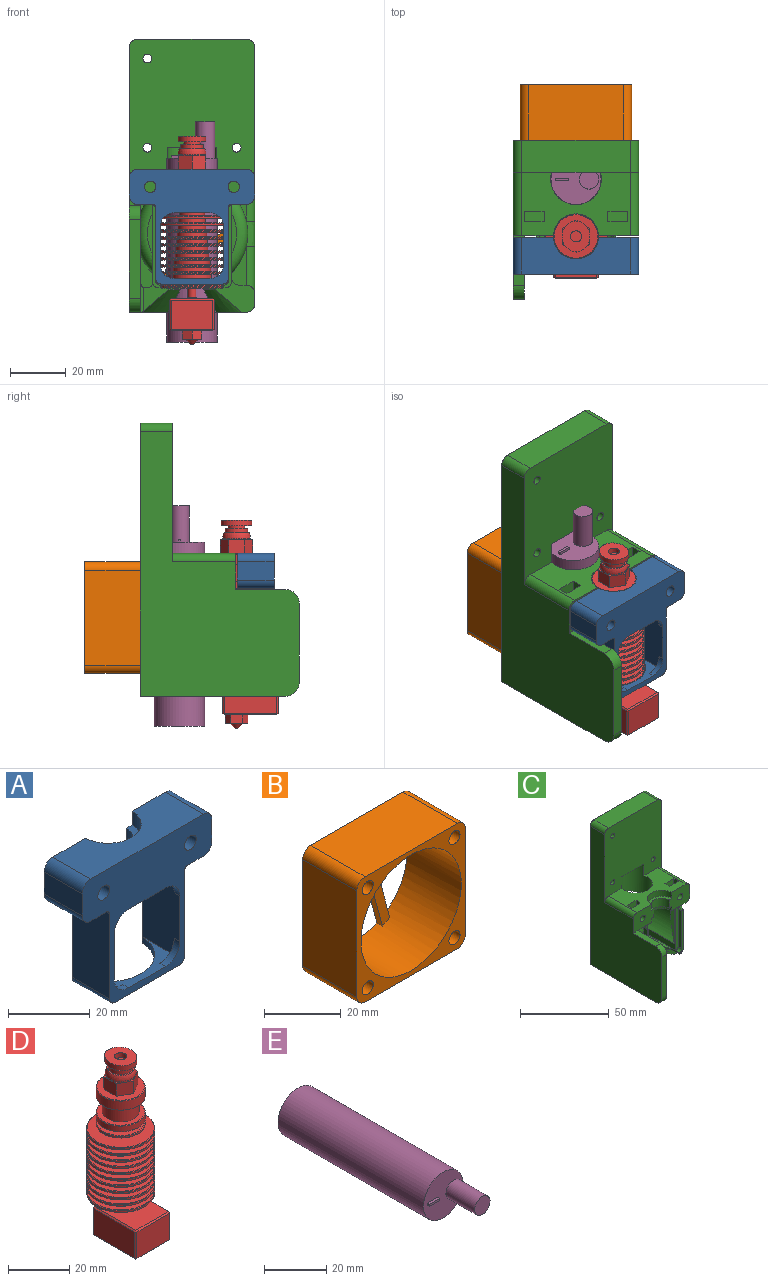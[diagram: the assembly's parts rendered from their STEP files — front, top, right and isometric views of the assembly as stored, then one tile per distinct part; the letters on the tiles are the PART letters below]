
ASSEMBLY  parts=5 mates=8
PART A: 39 faces, bbox 45x13.2x41.2 mm
  f0: plane 5x5mm, normal (0,1,0), area 5.4mm2, adj f15,f24,f26
  f1: plane 26.6x13mm, normal (1,0,0), area 319.8mm2, adj f2,f20,f21,f23,f24,f25,f27,f29
  f2: plane 39x13.2mm, normal (0,0,-1), area 303.4mm2, adj f1,f6,f11,f12,f15,f18,f20,f21
  f3: plane 39x13.2mm, normal (0,0,1), area 416.6mm2, adj f10,f11,f12,f21,f32,f33
  f4: plane 13.2x6.6mm, normal (1,0,0), area 87.1mm2, adj f11,f21,f31,f32
  f5: plane 13.2x6.6mm, normal (-1,0,0), area 87.1mm2, adj f12,f21,f33,f34
  f6: cylinder r=8.1mm len=16.19mm, axis (0,0,-1), area 67.1mm2, adj f2,f7,f11,f12
  f7: plane 16.19x7.8mm, normal (0,0,-1), area 43.4mm2, adj f6,f8,f11,f12
  f8: cylinder r=6.1mm len=12.19mm, axis (0,0,-1), area 107.7mm2, adj f7,f9,f11,f12
  f9: plane 16.19x7.8mm, normal (0,0,1), area 43.4mm2, adj f8,f10,f11,f12
  f10: cylinder r=8.1mm len=16.19mm, axis (0,0,-1), area 101.9mm2, adj f3,f9,f11,f12
  f11: plane 16.41x12.6mm, normal (0,1,0), area 176.1mm2, adj f2,f3,f4,f6,f7,f8,f9,f10
  f12: plane 16.41x12.6mm, normal (0,1,0), area 176.1mm2, adj f2,f3,f5,f6,f7,f8,f9,f10
  f13: cylinder r=2.05mm len=13.2mm, axis (0,-1,0), area 170mm2, adj f12,f21
  f14: cylinder r=2.05mm len=13.2mm, axis (0,-1,0), area 170mm2, adj f11,f21
  f15: plane 26.6x13mm, normal (-1,0,0), area 319.8mm2, adj f0,f2,f18,f21,f23,f24,f26,f28
  f16: plane 22x10.51mm, normal (0,0,-1), area 94.5mm2, adj f21,f30,f35,f36
  f17: plane 25.6x13mm, normal (1,0,0), area 332.8mm2, adj f18,f21,f36,f38
  f18: plane 28.56x2.61mm, normal (0,1,0), area 45.1mm2, adj f2,f15,f17,f24,f30,f36,f38
  f19: plane 25.6x13mm, normal (-1,0,0), area 332.8mm2, adj f20,f21,f35,f37
  f20: plane 28.56x2.61mm, normal (0,1,0), area 45.1mm2, adj f1,f2,f19,f24,f30,f35,f37
  f21: plane 45x41.2mm, normal (0,-1,0), area 758.6mm2, adj f1,f2,f3,f4,f5,f13,f14,f15
  f22: plane 12.8x2mm, normal (0,0,-1), area 25.6mm2, adj f21,f23,f28,f29
  f23: plane 22.8x8mm, normal (0,1,0), area 79.1mm2, adj f1,f2,f15,f22,f28,f29
  f24: plane 22.8x13mm, normal (0,0,1), area 83.7mm2, adj f0,f1,f15,f18,f20,f21,f25,f26
  f25: plane 5x5mm, normal (0,1,0), area 5.4mm2, adj f1,f24,f27
  f26: cylinder r=5mm len=5mm, axis (0,-1,0), area 15.7mm2, adj f0,f15,f21,f24
  f27: cylinder r=5mm len=5mm, axis (0,1,0), area 15.7mm2, adj f1,f21,f24,f25
  f28: cylinder r=5mm len=5mm, axis (0,1,0), area 15.7mm2, adj f15,f21,f22,f23
  f29: cylinder r=5mm len=5mm, axis (0,-1,0), area 15.7mm2, adj f1,f21,f22,f23
  f30: cylinder r=11.4mm len=22.78mm, axis (0,0,-1), area 69.5mm2, adj f16,f18,f20,f24,f35,f36
  f31: cylinder r=3mm len=13.2mm, axis (0,-1,0), area 62.2mm2, adj f2,f4,f11,f21
  f32: cylinder r=3mm len=13.2mm, axis (0,1,0), area 62.2mm2, adj f3,f4,f11,f21
  f33: cylinder r=3mm len=13.2mm, axis (0,-1,0), area 62.2mm2, adj f3,f5,f12,f21
  f34: cylinder r=3mm len=13.2mm, axis (0,1,0), area 62.2mm2, adj f2,f5,f12,f21
  f35: cylinder r=2mm len=13mm, axis (0,1,0), area 40.2mm2, adj f16,f19,f20,f21,f30
  f36: cylinder r=2mm len=13mm, axis (0,-1,0), area 40.2mm2, adj f16,f17,f18,f21,f30
  f37: cylinder r=1mm len=13mm, axis (0,-1,0), area 20.4mm2, adj f2,f19,f20,f21
  f38: cylinder r=1mm len=13mm, axis (0,1,0), area 20.4mm2, adj f2,f17,f18,f21
PART B: 25 faces, bbox 40x20x40 mm
  f0: plane 34x20mm, normal (0,0,-1), area 680mm2, adj f9,f10,f21,f24
  f1: plane 34x20mm, normal (1,0,0), area 680mm2, adj f9,f10,f21,f22
  f2: plane 34x20mm, normal (0,0,1), area 680mm2, adj f9,f10,f22,f23
  f3: cylinder r=18.5mm len=37mm, axis (0,1,0), area 2306.3mm2, adj f9,f10,f12,f13,f15,f16,f18,f19
  f4: cylinder r=2.05mm len=20mm, axis (0,1,0), area 257.6mm2, adj f9,f10
  f5: cylinder r=2.05mm len=20mm, axis (0,1,0), area 257.6mm2, adj f9,f10
  f6: cylinder r=2.05mm len=20mm, axis (0,1,0), area 257.6mm2, adj f9,f10
  f7: cylinder r=2.05mm len=20mm, axis (0,1,0), area 257.6mm2, adj f9,f10
  f8: plane 34x20mm, normal (-1,0,0), area 680mm2, adj f9,f10,f23,f24
  f9: plane 40x40mm, normal (0,-1,0), area 464.3mm2, adj f0,f1,f2,f3,f4,f5,f6,f7
  f10: plane 40x40mm, normal (0,1,0), area 702.9mm2, adj f0,f1,f2,f3,f4,f5,f6,f7
  f11: cylinder r=6mm len=5.91mm, axis (0,1,0), area 15.5mm2, adj f10,f12,f19,f20
  f12: plane 9.16x9.16mm, normal (0.71,0,-0.71), area 25.9mm2, adj f3,f10,f11,f20
  f13: plane 11.21x11.21mm, normal (-0.71,0,0.71), area 31.7mm2, adj f3,f10,f14,f20
  f14: cylinder r=6mm len=6.56mm, axis (0,1,0), area 15.5mm2, adj f10,f13,f15,f20
  f15: plane 12.52x3.35mm, normal (0.26,0,0.97), area 25.9mm2, adj f3,f10,f14,f20
  f16: plane 15.31x4.1mm, normal (-0.26,0,-0.97), area 31.7mm2, adj f3,f10,f17,f20
  f17: cylinder r=6mm len=7.2mm, axis (0,1,0), area 15.5mm2, adj f10,f16,f18,f20
  f18: plane 12.52x3.35mm, normal (-0.97,0,-0.26), area 25.9mm2, adj f3,f10,f17,f20
  f19: plane 15.31x4.1mm, normal (0.97,0,0.26), area 31.7mm2, adj f3,f10,f11,f20
  f20: plane 33.46x29.5mm, normal (0,-1,0), area 238.6mm2, adj f3,f11,f12,f13,f14,f15,f16,f17
  f21: cylinder r=3mm len=20mm, axis (0,-1,0), area 94.2mm2, adj f0,f1,f9,f10
  f22: cylinder r=3mm len=20mm, axis (0,1,0), area 94.2mm2, adj f1,f2,f9,f10
  f23: cylinder r=3mm len=20mm, axis (0,-1,0), area 94.2mm2, adj f2,f8,f9,f10
  f24: cylinder r=3mm len=20mm, axis (0,1,0), area 94.2mm2, adj f0,f8,f9,f10
PART C: 128 faces, bbox 46.5x61.4x99.5 mm
  f0: plane 11.9x4.4mm, normal (0,-1,0), area 34.1mm2, adj f2,f5,f11,f102,f122,f126
  f1: plane 10.46x9.18mm, normal (0,-1,0), area 42.6mm2, adj f5,f57,f80,f95,f100,f102,f125,f126
  f2: cylinder r=20mm len=22.2mm, axis (0,1,0), area 177mm2, adj f0,f4,f11,f122
  f3: cylinder r=20mm len=22.2mm, axis (0,1,0), area 72.4mm2, adj f4,f13,f14,f122
  f4: torus R=16mm, axis (0,-1,0), area 107.7mm2, adj f2,f3,f11,f13,f15,f20,f76,f99
  f5: plane 18.7x0.4mm, normal (0,0,1), area 7.5mm2, adj f0,f1,f102,f126
  f6: plane 98.6x45.6mm, normal (0,1,0), area 3336.5mm2, adj f8,f18,f38,f39,f61,f62,f63,f64
  f7: plane 39x22.7mm, normal (0,0,1), area 558.1mm2, adj f19,f20,f30,f32,f42,f43,f44,f45
  f8: plane 92x34.2mm, normal (1,0,0), area 979.4mm2, adj f6,f19,f85,f86,f87,f88,f89,f90
  f9: cylinder r=1.6mm len=4.4mm, axis (1,0,0), area 44.2mm2, adj f113,f114
  f10: plane 5x2.15mm, normal (-1,0,0), area 10.7mm2, adj f105,f106,f107,f111
  f11: plane 29.2x27.6mm, normal (-1,0,0), area 175mm2, adj f0,f2,f4,f15,f77,f95,f99,f102
  f12: plane 26.2x0.4mm, normal (1,0,0), area 10.5mm2, adj f13,f14,f20,f82
  f13: plane 26.2x8.43mm, normal (0,0,-1), area 95.2mm2, adj f3,f4,f12,f14,f20
  f14: plane 3.48x2.9mm, normal (0,-1,0), area 2.8mm2, adj f3,f12,f13,f82,f122
  f15: plane 15.13x1.9mm, normal (0,-1,0), area 19.4mm2, adj f4,f11
  f16: plane 15.13x1.9mm, normal (0,-1,0), area 19.4mm2, adj f68,f93
  f17: plane 6.06x2.48mm, normal (0,-1,0), area 6.3mm2, adj f24,f67,f86
  f18: plane 52x42mm, normal (0,0,-1), area 749.4mm2, adj f6,f38,f55,f60,f90,f100,f101,f108
  f19: plane 41.59x16.41mm, normal (0,-1,0), area 226.6mm2, adj f7,f8,f23,f24,f31,f32,f33,f34
  f20: plane 41.59x16.41mm, normal (0,-1,0), area 229.3mm2, adj f4,f7,f12,f13,f23,f32,f33,f34
  f21: plane 3.8x0.1mm, normal (0,1,0), area 0.2mm2, adj f61,f72
  f22: plane 18.7x2.4mm, normal (0,0,1), area 44.9mm2, adj f28,f60,f84,f89
  f23: plane 26.2x23.77mm, normal (0,0,-1), area 292.3mm2, adj f19,f20,f30,f36,f62,f65,f66,f69
  f24: plane 26.2x7.43mm, normal (0,0,-1), area 69mm2, adj f17,f19,f67,f85,f93
  f25: plane 24.37x7.02mm, normal (0,0,1), area 75mm2, adj f26,f55,f56,f57,f97
  f26: plane 4.56x3.93mm, normal (0,-1,0), area 11.3mm2, adj f25,f55,f61,f70,f97
  f27: plane 4.56x3.93mm, normal (0,-1,0), area 11.3mm2, adj f29,f55,f61,f65,f96
  f28: plane 14.06x5.4mm, normal (0,-1,0), area 41.8mm2, adj f22,f67,f68,f84,f88
  f29: plane 24.37x7.02mm, normal (0,0,1), area 75mm2, adj f27,f55,f58,f59,f96
  f30: cylinder r=9.1mm len=20.6mm, axis (0,0,1), area 886.5mm2, adj f7,f23,f62,f116,f127
  f31: cylinder r=2.05mm len=5mm, axis (0,-1,0), area 64.4mm2, adj f19,f46
  f32: cylinder r=8.1mm len=16.19mm, axis (0,0,-1), area 101.9mm2, adj f7,f19,f20,f33
  f33: plane 16.19x7.8mm, normal (0,0,1), area 43.4mm2, adj f19,f20,f32,f34
  f34: cylinder r=6.1mm len=12.19mm, axis (0,0,-1), area 107.7mm2, adj f19,f20,f33,f35
  f35: plane 16.19x7.8mm, normal (0,0,-1), area 43.4mm2, adj f19,f20,f34,f36
  f36: cylinder r=8.1mm len=16.19mm, axis (0,0,-1), area 67.1mm2, adj f19,f20,f23,f35
  f37: plane 10.34x3.7mm, normal (1,0,0), area 36.7mm2, adj f60,f89,f90,f115
  f38: plane 95x57mm, normal (-1,0,0), area 3051.4mm2, adj f6,f18,f20,f82,f83,f92,f116,f117
  f39: plane 39x11.5mm, normal (0,0,1), area 448.5mm2, adj f6,f91,f92,f116
  f40: cylinder r=2.05mm len=5mm, axis (0,-1,0), area 64.4mm2, adj f20,f43
  f41: plane 7.1x3.8mm, normal (0,0,1), area 27mm2, adj f42,f43,f44,f45
  f42: plane 10.8x3.8mm, normal (-1,0,0), area 41mm2, adj f7,f41,f43,f45
  f43: plane 10.8x7.1mm, normal (0,1,0), area 63.5mm2, adj f7,f40,f41,f42,f44
  f44: plane 10.8x3.8mm, normal (1,0,0), area 41mm2, adj f7,f41,f43,f45
  f45: plane 10.8x7.1mm, normal (0,-1,0), area 63.5mm2, adj f7,f41,f42,f44,f52
  f46: plane 10.8x7.1mm, normal (0,1,0), area 63.5mm2, adj f7,f31,f48,f49,f50
  f47: plane 10.8x7.1mm, normal (0,-1,0), area 63.5mm2, adj f7,f48,f49,f50,f54
  f48: plane 7.1x3.8mm, normal (0,0,1), area 27mm2, adj f46,f47,f49,f50
  f49: plane 10.8x3.8mm, normal (1,0,0), area 41mm2, adj f7,f46,f47,f48
  f50: plane 10.8x3.8mm, normal (-1,0,0), area 41mm2, adj f7,f46,f47,f48
  f51: plane 4.1x4.1mm, normal (0,-1,0), area 13.2mm2, adj f52
  f52: cylinder r=2.05mm len=4.1mm, axis (0,-1,0), area 30.9mm2, adj f45,f51
  f53: plane 4.1x4.1mm, normal (0,-1,0), area 13.2mm2, adj f54
  f54: cylinder r=2.05mm len=4.1mm, axis (0,-1,0), area 30.9mm2, adj f47,f53
  f55: cylinder r=9.1mm len=18.2mm, axis (0,0,1), area 333.8mm2, adj f18,f25,f26,f27,f29,f56,f58,f61
  f56: plane 7.52x4.9mm, normal (0.82,0.57,0), area 25.6mm2, adj f25,f55,f57,f100
  f57: cylinder r=11.4mm len=10.61mm, axis (0,0,-1), area 17.2mm2, adj f1,f25,f56,f80,f81,f97,f100
  f58: plane 7.52x4.9mm, normal (-0.82,0.57,0), area 25.6mm2, adj f29,f55,f59,f101
  f59: cylinder r=11.4mm len=10.61mm, axis (0,0,-1), area 17.2mm2, adj f29,f58,f60,f78,f79,f96,f101
  f60: plane 15.69x14.21mm, normal (0,-1,0), area 91.6mm2, adj f18,f22,f37,f59,f68,f78,f84,f89
  f61: cylinder r=18.5mm len=37mm, axis (0,-1,0), area 1412.8mm2, adj f6,f21,f26,f27,f55,f63,f64,f65
  f62: plane 23.77x8mm, normal (0,0.57,-0.82), area 151.8mm2, adj f6,f23,f30,f63,f64
  f63: bspline ~13.74x11.32mm, area 62.1mm2, adj f6,f61,f62,f66
  f64: bspline ~13.74x11.32mm, area 62.1mm2, adj f6,f61,f62,f69
  f65: plane 28.99x26.2mm, normal (-1,0,0), area 132.8mm2, adj f19,f23,f27,f61,f73,f96
  f66: extruded ~24.31x5.61mm, area 150.1mm2, adj f23,f61,f63,f73
  f67: cylinder r=20mm len=24.68mm, axis (0,1,0), area 595.4mm2, adj f17,f24,f28,f68,f87,f93
  f68: plane 29.2x27.6mm, normal (1,0,0), area 137.6mm2, adj f16,f28,f60,f67,f75,f84,f93,f94
  f69: extruded ~24.31x5.61mm, area 155.1mm2, adj f23,f61,f64,f72
  f70: plane 28.99x26.2mm, normal (1,0,0), area 132.8mm2, adj f20,f23,f26,f61,f72,f97
  f71: plane 3.8x0.1mm, normal (0,1,0), area 0.2mm2, adj f61,f73
  f72: plane 26.43x11.36mm, normal (0.82,0.57,0), area 231.6mm2, adj f21,f23,f61,f69,f70
  f73: plane 25.41x10.34mm, normal (-0.82,0.57,0), area 231.6mm2, adj f23,f61,f65,f66,f71
  f74: plane 25.61x3mm, normal (-1,0,0), area 76.8mm2, adj f19,f75,f93,f96,f98
  f75: plane 29.6x2.7mm, normal (0,-1,0), area 28.2mm2, adj f68,f74,f78,f79,f94,f96,f98
  f76: plane 25.61x3mm, normal (1,0,0), area 76.8mm2, adj f4,f20,f77,f97,f99
  f77: plane 29.6x2.7mm, normal (0,-1,0), area 28.2mm2, adj f11,f76,f80,f81,f95,f97,f99
  f78: plane 10.5x3.78mm, normal (0,0,-1), area 14.9mm2, adj f59,f60,f75,f79,f94
  f79: plane 2.7x1.01mm, normal (-1,0,0), area 2.7mm2, adj f59,f75,f78,f96
  f80: plane 10.5x3.78mm, normal (0,0,-1), area 14.9mm2, adj f1,f57,f77,f81,f95
  f81: plane 2.7x1.01mm, normal (1,0,0), area 2.7mm2, adj f57,f77,f80,f97
  f82: plane 44x4mm, normal (0,0,1), area 123.6mm2, adj f12,f14,f20,f38,f122,f124
  f83: plane 28.3x4mm, normal (0,-1,0), area 113.2mm2, adj f38,f122,f123,f124
  f84: cylinder r=3mm len=18.7mm, axis (0,1,0), area 88.1mm2, adj f22,f28,f60,f68
  f85: cylinder r=3mm len=29.2mm, axis (0,1,0), area 130.5mm2, adj f8,f19,f24,f86
  f86: cylinder r=3mm len=9.06mm, axis (0,0,-1), area 35.6mm2, adj f8,f17,f85,f87
  f87: bspline ~11.65x3.39mm, area 38.9mm2, adj f8,f67,f86,f88
  f88: cylinder r=3mm len=17.06mm, axis (0,0,-1), area 73.3mm2, adj f8,f28,f87,f89
  f89: cylinder r=3mm len=21.7mm, axis (0,-1,0), area 92.4mm2, adj f8,f22,f37,f60,f88,f115
  f90: cylinder r=3mm len=26.7mm, axis (0,-1,0), area 122mm2, adj f6,f8,f18,f37,f60,f115
  f91: cylinder r=3mm len=11.5mm, axis (0,1,0), area 54.2mm2, adj f6,f8,f39,f116
  f92: cylinder r=3mm len=11.5mm, axis (0,-1,0), area 54.2mm2, adj f6,f38,f39,f116
  f93: torus R=16mm, axis (0,-1,0), area 150.7mm2, adj f16,f19,f24,f67,f68,f74,f98
  f94: cylinder r=2mm len=10.5mm, axis (0,1,0), area 33mm2, adj f60,f68,f75,f78
  f95: cylinder r=2mm len=10.5mm, axis (0,1,0), area 33mm2, adj f1,f11,f77,f80
  f96: cylinder r=2mm len=29.2mm, axis (0,1,0), area 13.9mm2, adj f19,f27,f29,f59,f65,f74,f75,f79
  f97: cylinder r=2mm len=29.2mm, axis (0,-1,0), area 13.9mm2, adj f20,f25,f26,f57,f70,f76,f77,f81
  f98: cylinder r=1mm len=3.23mm, axis (0,-1,0), area 4.6mm2, adj f68,f74,f75,f93
  f99: cylinder r=1mm len=3.23mm, axis (0,-1,0), area 4.6mm2, adj f4,f11,f76,f77
  f100: cone r=11.4mm half-angle=45deg, axis (0,0,-1), area 105.5mm2, adj f1,f18,f55,f56,f57,f125
  f101: cone r=11.4mm half-angle=45deg, axis (0,0,-1), area 99.4mm2, adj f18,f55,f58,f59,f60
  f102: cylinder r=2mm len=18.7mm, axis (0,-1,0), area 58.8mm2, adj f0,f1,f5,f11
  f103: plane 5x4mm, normal (0,1,0), area 20mm2, adj f55,f104,f106,f107
  f104: plane 5x2.15mm, normal (-1,0,0), area 10.7mm2, adj f103,f106,f107,f112
  f105: plane 5x4mm, normal (0,-1,0), area 20mm2, adj f10,f55,f106,f107
  f106: plane 10x4mm, normal (0,0,-1), area 29.8mm2, adj f10,f55,f103,f104,f105,f110
  f107: plane 10x4mm, normal (0,0,1), area 29.8mm2, adj f10,f55,f103,f104,f105,f108
  f108: plane 5.7x2.35mm, normal (1,0,0), area 13.4mm2, adj f18,f107,f111,f112
  f109: plane 5.7x2.5mm, normal (0,0,-1), area 14.3mm2, adj f110,f111,f112,f113
  f110: plane 5.7x2.35mm, normal (1,0,0), area 13.4mm2, adj f106,f109,f111,f112
  f111: plane 9.7x2.5mm, normal (0,-1,0), area 24.3mm2, adj f10,f18,f108,f109,f110,f113
  f112: plane 9.7x2.5mm, normal (0,1,0), area 24.3mm2, adj f18,f104,f108,f109,f110,f113
  f113: plane 9.7x5.7mm, normal (-1,0,0), area 47.2mm2, adj f9,f18,f109,f111,f112
  f114: plane 6x6mm, normal (1,0,0), area 20.2mm2, adj f9,f115
  f115: cylinder r=3mm len=6mm, axis (1,0,0), area 74.8mm2, adj f8,f37,f89,f90,f114
  f116: plane 49.7x45mm, normal (0,-1,0), area 1937.4mm2, adj f7,f8,f30,f38,f39,f91,f92,f117
  f117: cylinder r=3mm len=22.7mm, axis (0,1,0), area 107mm2, adj f7,f20,f38,f116
  f118: cylinder r=3mm len=22.7mm, axis (0,-1,0), area 107mm2, adj f7,f8,f19,f116
  f119: cylinder r=1.6mm len=11.5mm, axis (0,1,0), area 115.6mm2, adj f6,f116
  f120: cylinder r=1.6mm len=11.5mm, axis (0,1,0), area 115.6mm2, adj f6,f116
  f121: cylinder r=1.6mm len=11.5mm, axis (0,1,0), area 115.6mm2, adj f6,f116
  f122: plane 49x38.3mm, normal (1,0,0), area 1279.6mm2, adj f0,f2,f3,f4,f14,f18,f82,f83
  f123: cylinder r=5mm len=5mm, axis (1,0,0), area 31.4mm2, adj f18,f38,f83,f122
  f124: cylinder r=5mm len=5mm, axis (-1,0,0), area 31.4mm2, adj f38,f82,f83,f122
  f125: cylinder r=1mm len=10.7mm, axis (0,0,1), area 15.4mm2, adj f1,f18,f100,f122,f126
  f126: cylinder r=2mm len=19.7mm, axis (0,1,0), area 59.8mm2, adj f0,f1,f5,f122,f125
  f127: plane 17.5x6.6mm, normal (0,0,-1), area 85.2mm2, adj f30,f116
PART D: 145 faces, bbox 22.3x26.2x74.9 mm
  f0: plane 4.33x2.5mm, normal (0,0,1), area 1.3mm2, adj f130,f131,f134
  f1: plane 5x1.44mm, normal (0,0,1), area 1.3mm2, adj f129,f130,f134
  f2: plane 4.33x2.5mm, normal (0,0,1), area 1.3mm2, adj f128,f129,f134
  f3: plane 4.33x2.5mm, normal (0,0,1), area 1.3mm2, adj f127,f128,f134
  f4: plane 5x1.44mm, normal (0,0,1), area 1.3mm2, adj f127,f132,f134
  f5: plane 19x15mm, normal (0,0,-1), area 242.6mm2, adj f103,f108,f111,f114,f116,f117,f118,f119
  f6: plane 15.6x15.6mm, normal (0,0,1), area 104.5mm2, adj f89,f127,f128,f129,f130,f131,f132
  f7: cylinder r=1.5mm len=3.3mm, axis (0,0,-1), area 31.1mm2, adj f8,f115
  f8: plane 21.9x21.9mm, normal (0,0,-1), area 369.6mm2, adj f7,f62
  f9: cylinder r=11.15mm len=22.3mm, axis (0,0,-1), area 42mm2, adj f62,f63
  f10: plane 21.9x21.9mm, normal (0,0,1), area 200mm2, adj f11,f63
  f11: cylinder r=7.5mm len=15mm, axis (0,0,-1), area 70.7mm2, adj f10,f12
  f12: plane 21.9x21.9mm, normal (0,0,-1), area 200mm2, adj f11,f64
  f13: cylinder r=11.15mm len=22.3mm, axis (0,0,-1), area 42mm2, adj f64,f65
  f14: plane 21.9x21.9mm, normal (0,0,1), area 222.7mm2, adj f15,f65
  f15: cylinder r=7mm len=14mm, axis (0,0,-1), area 66mm2, adj f14,f16
  f16: plane 21.9x21.9mm, normal (0,0,-1), area 222.7mm2, adj f15,f66
  f17: cylinder r=11.15mm len=22.3mm, axis (0,0,-1), area 42mm2, adj f66,f67
  f18: plane 21.9x21.9mm, normal (0,0,1), area 233.5mm2, adj f19,f67
  f19: cylinder r=6.75mm len=13.5mm, axis (0,0,-1), area 63.6mm2, adj f18,f20
  f20: plane 21.9x21.9mm, normal (0,0,-1), area 233.5mm2, adj f19,f68
  f21: cylinder r=11.15mm len=22.3mm, axis (0,0,-1), area 42mm2, adj f68,f69
  f22: plane 21.9x21.9mm, normal (0,0,1), area 244mm2, adj f23,f69
  f23: cylinder r=6.5mm len=13mm, axis (0,0,-1), area 61.3mm2, adj f22,f24
  f24: plane 21.9x21.9mm, normal (0,0,-1), area 244mm2, adj f23,f70
  f25: cylinder r=11.15mm len=22.3mm, axis (0,0,-1), area 42mm2, adj f70,f71
  f26: plane 21.9x21.9mm, normal (0,0,1), area 263.6mm2, adj f27,f71
  f27: cylinder r=6mm len=12mm, axis (0,0,-1), area 56.5mm2, adj f26,f28
  f28: plane 21.9x21.9mm, normal (0,0,-1), area 263.6mm2, adj f27,f72
  f29: cylinder r=11.15mm len=22.3mm, axis (0,0,-1), area 42mm2, adj f72,f73
  f30: plane 21.9x21.9mm, normal (0,0,1), area 272.8mm2, adj f31,f73
  f31: cylinder r=5.75mm len=11.5mm, axis (0,0,-1), area 54.2mm2, adj f30,f32
  f32: plane 21.9x21.9mm, normal (0,0,-1), area 272.8mm2, adj f31,f74
  f33: cylinder r=11.15mm len=22.3mm, axis (0,0,-1), area 42mm2, adj f74,f75
  f34: plane 21.9x21.9mm, normal (0,0,1), area 281.7mm2, adj f35,f75
  f35: cylinder r=5.5mm len=11mm, axis (0,0,-1), area 51.8mm2, adj f34,f36
  f36: plane 21.9x21.9mm, normal (0,0,-1), area 281.7mm2, adj f35,f76
  f37: cylinder r=11.15mm len=22.3mm, axis (0,0,-1), area 42mm2, adj f76,f77
  f38: plane 21.9x21.9mm, normal (0,0,1), area 290.1mm2, adj f39,f77
  f39: cylinder r=5.25mm len=10.5mm, axis (0,0,-1), area 49.5mm2, adj f38,f40
  f40: plane 21.9x21.9mm, normal (0,0,-1), area 290.1mm2, adj f39,f78
  f41: cylinder r=11.15mm len=22.3mm, axis (0,0,-1), area 42mm2, adj f78,f79
  f42: plane 21.9x21.9mm, normal (0,0,1), area 298.1mm2, adj f43,f79
  f43: cylinder r=5mm len=10mm, axis (0,0,-1), area 47.1mm2, adj f42,f44
  f44: plane 21.9x21.9mm, normal (0,0,-1), area 298.1mm2, adj f43,f80
  f45: cylinder r=11.15mm len=22.3mm, axis (0,0,-1), area 42mm2, adj f80,f81
  f46: plane 21.9x21.9mm, normal (0,0,1), area 305.8mm2, adj f47,f81
  f47: cylinder r=4.75mm len=9.5mm, axis (0,0,-1), area 44.8mm2, adj f46,f48
  f48: plane 21.9x21.9mm, normal (0,0,-1), area 305.8mm2, adj f47,f82
  f49: cylinder r=11.15mm len=22.3mm, axis (0,0,-1), area 42mm2, adj f82,f83
  f50: plane 21.9x21.9mm, normal (0,0,1), area 313.1mm2, adj f51,f83
  f51: cylinder r=4.5mm len=9mm, axis (0,0,-1), area 42.4mm2, adj f50,f52
  f52: plane 15.6x15.6mm, normal (0,0,-1), area 127.5mm2, adj f51,f84
  f53: cylinder r=8mm len=16mm, axis (0,0,-1), area 30.2mm2, adj f84,f85
  f54: plane 15.6x15.6mm, normal (0,0,1), area 127.5mm2, adj f55,f85
  f55: cylinder r=4.5mm len=9mm, axis (0,0,-1), area 42.4mm2, adj f54,f56
  f56: plane 15.6x15.6mm, normal (0,0,-1), area 127.5mm2, adj f55,f86
  f57: cylinder r=8mm len=16mm, axis (0,0,-1), area 110.6mm2, adj f86,f87
  f58: plane 15.6x15.6mm, normal (0,0,1), area 78mm2, adj f59,f87
  f59: cylinder r=6mm len=12mm, axis (0,0,-1), area 226.2mm2, adj f58,f60
  f60: plane 15.6x15.6mm, normal (0,0,-1), area 78mm2, adj f59,f88
  f61: cylinder r=8mm len=16mm, axis (0,0,-1), area 181mm2, adj f88,f89
  f62: cone r=10.95mm half-angle=45deg, axis (0,0,1), area 19.6mm2, adj f8,f9
  f63: cone r=11.15mm half-angle=45deg, axis (0,0,-1), area 19.6mm2, adj f9,f10
  f64: cone r=10.95mm half-angle=45deg, axis (0,0,1), area 19.6mm2, adj f12,f13
  f65: cone r=11.15mm half-angle=45deg, axis (0,0,-1), area 19.6mm2, adj f13,f14
  f66: cone r=10.95mm half-angle=45deg, axis (0,0,1), area 19.6mm2, adj f16,f17
  f67: cone r=11.15mm half-angle=45deg, axis (0,0,-1), area 19.6mm2, adj f17,f18
  f68: cone r=10.95mm half-angle=45deg, axis (0,0,1), area 19.6mm2, adj f20,f21
  f69: cone r=11.15mm half-angle=45deg, axis (0,0,-1), area 19.6mm2, adj f21,f22
  f70: cone r=10.95mm half-angle=45deg, axis (0,0,1), area 19.6mm2, adj f24,f25
  f71: cone r=11.15mm half-angle=45deg, axis (0,0,-1), area 19.6mm2, adj f25,f26
  f72: cone r=10.95mm half-angle=45deg, axis (0,0,1), area 19.6mm2, adj f28,f29
  f73: cone r=11.15mm half-angle=45deg, axis (0,0,-1), area 19.6mm2, adj f29,f30
  f74: cone r=10.95mm half-angle=45deg, axis (0,0,1), area 19.6mm2, adj f32,f33
  f75: cone r=11.15mm half-angle=45deg, axis (0,0,-1), area 19.6mm2, adj f33,f34
  f76: cone r=10.95mm half-angle=45deg, axis (0,0,1), area 19.6mm2, adj f36,f37
  f77: cone r=11.15mm half-angle=45deg, axis (0,0,-1), area 19.6mm2, adj f37,f38
  f78: cone r=10.95mm half-angle=45deg, axis (0,0,1), area 19.6mm2, adj f40,f41
  f79: cone r=11.15mm half-angle=45deg, axis (0,0,-1), area 19.6mm2, adj f41,f42
  f80: cone r=10.95mm half-angle=45deg, axis (0,0,1), area 19.6mm2, adj f44,f45
  f81: cone r=11.15mm half-angle=45deg, axis (0,0,-1), area 19.6mm2, adj f45,f46
  f82: cone r=10.95mm half-angle=45deg, axis (0,0,1), area 19.6mm2, adj f48,f49
  f83: cone r=11.15mm half-angle=45deg, axis (0,0,-1), area 19.6mm2, adj f49,f50
  f84: cone r=7.8mm half-angle=45deg, axis (0,0,1), area 14mm2, adj f52,f53
  f85: cone r=8mm half-angle=45deg, axis (0,0,-1), area 14mm2, adj f53,f54
  f86: cone r=7.8mm half-angle=45deg, axis (0,0,1), area 14mm2, adj f56,f57
  f87: cone r=8mm half-angle=45deg, axis (0,0,-1), area 14mm2, adj f57,f58
  f88: cone r=7.8mm half-angle=45deg, axis (0,0,1), area 14mm2, adj f60,f61
  f89: cone r=8mm half-angle=45deg, axis (0,0,-1), area 14mm2, adj f6,f61
  f90: plane 15x10.5mm, normal (0,1,0), area 157.5mm2, adj f98,f99,f108,f109
  f91: plane 19x10.5mm, normal (1,0,0), area 199.5mm2, adj f95,f98,f102,f103
  f92: plane 15x10.5mm, normal (0,-1,0), area 157.5mm2, adj f101,f102,f110,f111
  f93: plane 19x10.5mm, normal (-1,0,0), area 199.5mm2, adj f100,f109,f110,f114
  f94: plane 19x15mm, normal (0,0,1), area 272.4mm2, adj f95,f99,f100,f101,f115
  f95: plane 19x0.5mm, normal (0.71,0,0.71), area 13.4mm2, adj f91,f94,f96,f97
  f96: plane 0.5x0.5mm, normal (0.58,0.58,0.58), area 0.2mm2, adj f95,f98,f99
  f97: plane 0.5x0.5mm, normal (0.58,-0.58,0.58), area 0.2mm2, adj f95,f101,f102
  f98: plane 10.5x0.5mm, normal (0.71,0.71,0), area 7.4mm2, adj f90,f91,f96,f104
  f99: plane 15x0.5mm, normal (0,0.71,0.71), area 10.6mm2, adj f90,f94,f96,f105
  f100: plane 19x0.5mm, normal (-0.71,0,0.71), area 13.4mm2, adj f93,f94,f105,f106
  f101: plane 15x0.5mm, normal (0,-0.71,0.71), area 10.6mm2, adj f92,f94,f97,f106
  f102: plane 10.5x0.5mm, normal (0.71,-0.71,0), area 7.4mm2, adj f91,f92,f97,f107
  f103: plane 19x0.5mm, normal (0.71,0,-0.71), area 13.4mm2, adj f5,f91,f104,f107
  f104: plane 0.5x0.5mm, normal (0.58,0.58,-0.58), area 0.2mm2, adj f98,f103,f108
  f105: plane 0.5x0.5mm, normal (-0.58,0.58,0.58), area 0.2mm2, adj f99,f100,f109
  f106: plane 0.5x0.5mm, normal (-0.58,-0.58,0.58), area 0.2mm2, adj f100,f101,f110
  f107: plane 0.5x0.5mm, normal (0.58,-0.58,-0.58), area 0.2mm2, adj f102,f103,f111
  f108: plane 15x0.5mm, normal (0,0.71,-0.71), area 10.6mm2, adj f5,f90,f104,f112
  f109: plane 10.5x0.5mm, normal (-0.71,0.71,0), area 7.4mm2, adj f90,f93,f105,f112
  f110: plane 10.5x0.5mm, normal (-0.71,-0.71,0), area 7.4mm2, adj f92,f93,f106,f113
  f111: plane 15x0.5mm, normal (0,-0.71,-0.71), area 10.6mm2, adj f5,f92,f107,f113
  f112: plane 0.5x0.5mm, normal (-0.58,0.58,-0.58), area 0.2mm2, adj f108,f109,f114
  f113: plane 0.5x0.5mm, normal (-0.58,-0.58,-0.58), area 0.2mm2, adj f110,f111,f114
  f114: plane 19x0.5mm, normal (-0.71,0,-0.71), area 13.4mm2, adj f5,f93,f112,f113
  f115: cone r=2mm half-angle=45deg, axis (0,0,-1), area 7.8mm2, adj f7,f94
  f116: plane 3.5x3mm, normal (0.5,0.87,0), area 12.1mm2, adj f5,f117,f121,f122
  f117: plane 4.04x3mm, normal (1,0,0), area 12.1mm2, adj f5,f116,f118,f122
  f118: plane 3.5x3mm, normal (0.5,-0.87,0), area 12.1mm2, adj f5,f117,f119,f122
  f119: plane 3.5x3mm, normal (-0.5,-0.87,0), area 12.1mm2, adj f5,f118,f120,f122
  f120: plane 4.04x3mm, normal (-1,0,0), area 12.1mm2, adj f5,f119,f121,f122
  f121: plane 3.5x3mm, normal (-0.5,0.87,0), area 12.1mm2, adj f5,f116,f120,f122
  f122: plane 8.08x7mm, normal (0,0,-1), area 26.5mm2, adj f116,f117,f118,f119,f120,f121,f123
  f123: cone r=0.5mm half-angle=41.2deg, axis (0,0,1), area 23mm2, adj f122,f124
  f124: plane 1x1mm, normal (0,0,-1), area 0.7mm2, adj f123,f125
  f125: cylinder r=0.2mm len=1.8mm, axis (0,0,1), area 2.3mm2, adj f124,f126
  f126: plane 0.4x0.4mm, normal (0,0,-1), area 0.1mm2, adj f125
  f127: plane 5x5mm, normal (0.5,-0.87,0), area 28.9mm2, adj f3,f4,f6,f128,f132
  f128: plane 5.77x5mm, normal (1,0,0), area 28.9mm2, adj f2,f3,f6,f127,f129
  f129: plane 5x5mm, normal (0.5,0.87,0), area 28.9mm2, adj f1,f2,f6,f128,f130
  f130: plane 5x5mm, normal (-0.5,0.87,0), area 28.9mm2, adj f0,f1,f6,f129,f131
  f131: plane 5.77x5mm, normal (-1,0,0), area 28.9mm2, adj f0,f6,f130,f132,f133
  f132: plane 5x5mm, normal (-0.5,-0.87,0), area 28.9mm2, adj f4,f6,f127,f131,f133
  f133: plane 4.33x2.5mm, normal (0,0,1), area 1.3mm2, adj f131,f132,f134
  f134: cylinder r=5mm len=10mm, axis (0,0,-1), area 15.7mm2, adj f0,f1,f2,f3,f4,f133,f135
  f135: torus R=0.75mm, axis (0,0,-1), area 63.2mm2, adj f134,f136
  f136: plane 9x9mm, normal (0,0,1), area 13.4mm2, adj f135,f137
  f137: cylinder r=4mm len=8mm, axis (0,0,-1), area 37.7mm2, adj f136,f138
  f138: plane 8x8mm, normal (0,0,1), area 22mm2, adj f137,f139
  f139: cylinder r=3mm len=6mm, axis (0,0,-1), area 18.8mm2, adj f138,f143
  f140: extruded ~11x10mm, area 66mm2, adj f142,f143
  f141: cylinder r=2mm len=4mm, axis (0,0,-1), area 25.1mm2, adj f142,f144
  f142: plane 11x10mm, normal (0,0,1), area 73.8mm2, adj f140,f141
  f143: plane 11x10mm, normal (0,0,-1), area 58.1mm2, adj f139,f140
  f144: plane 4x4mm, normal (0,0,1), area 12.6mm2, adj f141
PART E: 10 faces, bbox 18x79x18 mm
  f0: cylinder r=9mm len=66mm, axis (0,1,0), area 3732.2mm2, adj f1,f2
  f1: plane 18x18mm, normal (0,-1,0), area 212.1mm2, adj f0,f3,f5,f6,f7,f8
  f2: plane 18x18mm, normal (0,1,0), area 254.5mm2, adj f0
  f3: cylinder r=3.5mm len=13mm, axis (0,1,0), area 285.9mm2, adj f1,f4
  f4: plane 7x7mm, normal (0,-1,0), area 38.5mm2, adj f3
  f5: plane 4.74x1mm, normal (0,0,-1), area 4.7mm2, adj f1,f6,f8,f9
  f6: plane 1x0.82mm, normal (1,0,0), area 0.8mm2, adj f1,f5,f7,f9
  f7: plane 4.74x1mm, normal (0,0,1), area 4.7mm2, adj f1,f6,f8,f9
  f8: plane 1x0.82mm, normal (-1,0,0), area 0.8mm2, adj f1,f5,f7,f9
  f9: plane 4.74x0.82mm, normal (0,-1,0), area 3.9mm2, adj f5,f6,f7,f8
PLACE A rot(axis=(0,0,1),0deg) t=(-6.27,-7.94,12.47)mm
PLACE B rot(axis=(0,0,-1),180deg) t=(-6.27,26.56,-4.33)mm
PLACE C rot(axis=(0,0,1),0deg) t=(-86.27,-7.94,12.47)mm fixed
PLACE D rot(axis=(0,0,1),0deg) t=(-6.27,-7.94,-27.73)mm
PLACE E rot(axis=(-1,0,0),90deg) t=(-6.27,12.56,-43.23)mm
MATE parallel A.f21 <-> C.f19  axis (0,-1,0) through (-6.27,-21.44,6.72)mm
MATE revolute C.f2 <-> B.f3  axis (0,1,0) through (-6.27,26.56,-4.33)mm
MATE slider E.f0 <-> C.f30  axis (0,0,1) through (-6.27,12.56,22.77)mm
MATE planar E.f0 <-> D.f7  axis (0,0,-1) through (-6.27,12.56,-43.23)mm
MATE parallel D.f92 <-> C.f116  axis (0,-1,0) through (-6.27,-22.94,-33.48)mm
MATE parallel B.f8 <-> C.f8  axis (1,0,0) through (13.73,36.56,-4.33)mm
MATE revolute A.f6 <-> D.f7  axis (0,0,1) through (-6.27,-7.94,14.67)mm
MATE revolute D.f7 <-> C.f32  axis (0,0,-1) through (-6.27,-7.94,14.67)mm
